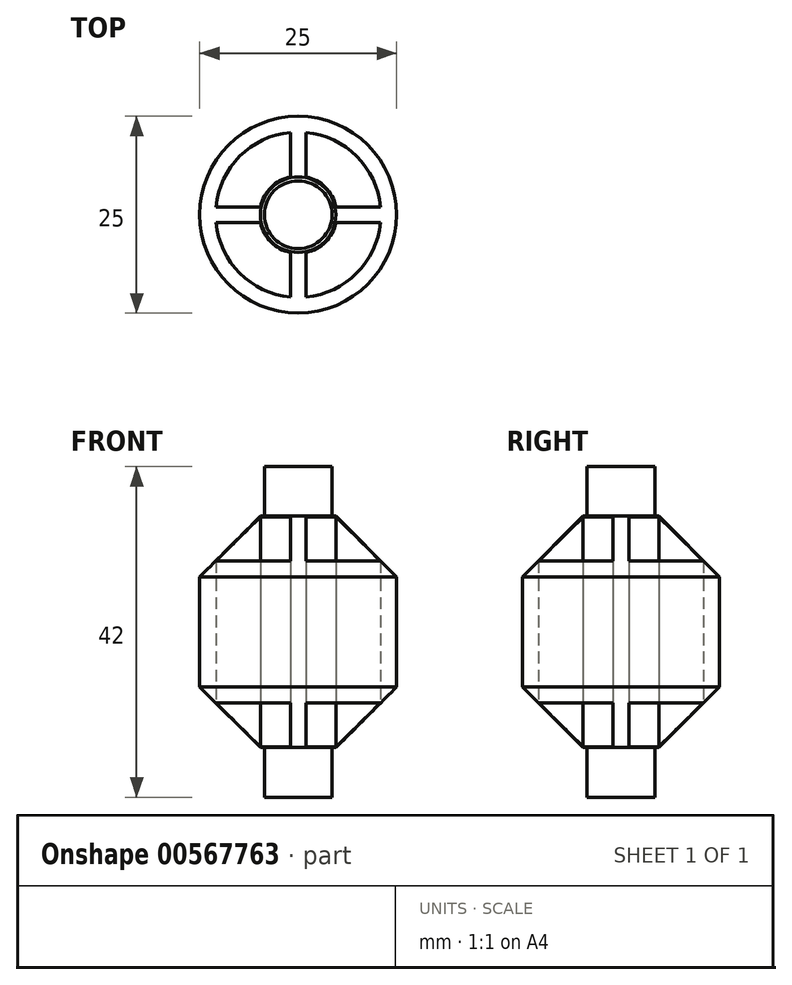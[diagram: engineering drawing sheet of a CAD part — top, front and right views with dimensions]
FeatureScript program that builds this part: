
annotation { "Feature Type Name" : "Feature", "Feature Type Description" : "" }
export const myFeature = defineFeature(function(context is Context, id is Id, definition is map)
    precondition{}
    {
        {
            var Q0;
            Q0=qCreatedBy(makeId("Top.planeOp"),FACE);
            var sketch = newSketch(context, id + "F0", { "sketchPlane" : qUnion([Q0])});
            skCircle(sketch, "E0", {"center": v(0, 0) * mm, "radius": 4.3 * mm});
            skCircle(sketch, "E1", {"center": v(0, 0) * mm, "radius": 2.3 * mm});
            skCircle(sketch, "E2", {"center": v(0, 0) * mm, "radius": 4.9 * mm});
            skCircle(sketch, "E3", {"center": v(0, 0) * mm, "radius": 12.5 * mm});
            skCircle(sketch, "E4", {"center": v(0, 0) * mm, "radius": 10.5 * mm});
            skLineSegment(sketch, "E5", {"start": v(-1, 4.8) * mm, "end": v(-1, 10.45) * mm});
            skLineSegment(sketch, "E6", {"start": v(1, 4.8) * mm, "end": v(1, 10.45) * mm});
            skLineSegment(sketch, "E7.1.0", {"start": v(-4.8, 1) * mm, "end": v(-10.45, 1) * mm});
            skLineSegment(sketch, "E7.1.1", {"start": v(-4.8, -1) * mm, "end": v(-10.45, -1) * mm});
            skLineSegment(sketch, "E7.2.0", {"start": v(-1, -4.8) * mm, "end": v(-1, -10.45) * mm});
            skLineSegment(sketch, "E7.2.1", {"start": v(1, -4.8) * mm, "end": v(1, -10.45) * mm});
            skLineSegment(sketch, "E7.3.0", {"start": v(4.8, -1) * mm, "end": v(10.45, -1) * mm});
            skLineSegment(sketch, "E7.3.1", {"start": v(4.8, 1) * mm, "end": v(10.45, 1) * mm});
            skSolve(sketch);
        }
        {
            var Q0;
            Q0=makeQuery(id+"F0.imprint","IMPRINT",FACE,{"disambiguationData":[TD([[makeQuery(id+"F0.imprint","IMPRINT",EDGE,{"derivedFrom":sQuery(id+"F0.wireOp",EDGE,"E0")}),1.0]])]});
            var Q1;
            Q1=makeQuery(id+"F0.imprint","IMPRINT",FACE,{"disambiguationData":[TD([[makeQuery(id+"F0.imprint","IMPRINT",EDGE,{"derivedFrom":sQuery(id+"F0.wireOp",EDGE,"E1")}),1.0]])]});
            extrude(context, id + "F1", {"entities" : qUnion([Q0, Q1]), "endBound" : BoundingType.SYMMETRIC, "depth" : 42 * mm, "offsetDistance" : 25 * mm});
        }
        {
            var Q0;
            Q0=makeQuery(id+"F0.imprint","IMPRINT",FACE,{"disambiguationData":[TD([[makeQuery(id+"F0.imprint","IMPRINT",EDGE,{"derivedFrom":sQuery(id+"F0.wireOp",EDGE,"E0")}),-1.0]])]});
            var Q1;
            {var subQ0=sQuery(id+"F0.wireOp",EDGE,"E7.1.0");Q1=makeQuery(id+"F0.imprint","IMPRINT",FACE,{"disambiguationData":[TD([[makeQuery(id+"F0.imprint","IMPRINT",EDGE,{"derivedFrom":subQ0}),1.0]])]});}
            var Q2;
            {var subQ0=sQuery(id+"F0.wireOp",EDGE,"E7.2.0");Q2=makeQuery(id+"F0.imprint","IMPRINT",FACE,{"disambiguationData":[TD([[makeQuery(id+"F0.imprint","IMPRINT",EDGE,{"derivedFrom":subQ0}),1.0]])]});}
            var Q3;
            {var subQ0=sQuery(id+"F0.wireOp",EDGE,"E7.3.0");Q3=makeQuery(id+"F0.imprint","IMPRINT",FACE,{"disambiguationData":[TD([[makeQuery(id+"F0.imprint","IMPRINT",EDGE,{"derivedFrom":subQ0}),1.0]])]});}
            var Q4;
            Q4=makeQuery(id+"F0.imprint","IMPRINT",FACE,{"disambiguationData":[TD([[makeQuery(id+"F0.imprint","IMPRINT",EDGE,{"derivedFrom":sQuery(id+"F0.wireOp",EDGE,"E3")}),1.0]])]});
            var Q5;
            {var subQ0=sQuery(id+"F0.wireOp",EDGE,"E5");Q5=makeQuery(id+"F0.imprint","IMPRINT",FACE,{"disambiguationData":[TD([[makeQuery(id+"F0.imprint","IMPRINT",EDGE,{"derivedFrom":subQ0}),-1.0]])]});}
            extrude(context, id + "F2", {"entities" : qUnion([Q0, Q1, Q2, Q3, Q4, Q5]), "operationType" : NewBodyOperationType.ADD, "endBound" : BoundingType.SYMMETRIC, "depth" : 29.4 * mm, "offsetDistance" : 25 * mm});
        }
        {
            var Q0;
            Q0=qCreatedBy(makeId("Front.planeOp"),FACE);
            var sketch = newSketch(context, id + "F3", { "sketchPlane" : qUnion([Q0])});
            skPoint(sketch, "E8.0", {"position": v(-4.8, 14.7) * mm});
            skPoint(sketch, "E8.1", {"position": v(-4.8, -14.7) * mm});
            skLineSegment(sketch, "E9", {"start": v(-4.8, -14.7) * mm, "end": v(-13.43, -6.07) * mm});
            skLineSegment(sketch, "E10", {"start": v(-13.43, -6.07) * mm, "end": v(-13.43, 6.07) * mm});
            skLineSegment(sketch, "E11", {"start": v(-13.43, 6.07) * mm, "end": v(-4.8, 14.7) * mm});
            skLineSegment(sketch, "E12", {"start": v(-4.8, -14.7) * mm, "end": v(-4.8, 14.7) * mm, "construction": true});
            skLineSegment(sketch, "E13", {"start": v(-13.43, -6.07) * mm, "end": v(-13.43, -14.7) * mm});
            skLineSegment(sketch, "E14", {"start": v(-13.43, -14.7) * mm, "end": v(-4.8, -14.7) * mm});
            skLineSegment(sketch, "E15", {"start": v(-13.43, 6.07) * mm, "end": v(-13.43, 14.7) * mm});
            skLineSegment(sketch, "E16", {"start": v(-13.43, 14.7) * mm, "end": v(-4.8, 14.7) * mm});
            skSolve(sketch);
        }
        {
            var Q0;
            Q0=makeQuery(id+"F3.imprint","IMPRINT",FACE,{"disambiguationData":[TD([[makeQuery(id+"F3.imprint","IMPRINT",EDGE,{"derivedFrom":sQuery(id+"F3.wireOp",EDGE,"E11")}),1.0]])]});
            var Q1;
            Q1=makeQuery(id+"F3.imprint","IMPRINT",FACE,{"disambiguationData":[TD([[makeQuery(id+"F3.imprint","IMPRINT",EDGE,{"derivedFrom":sQuery(id+"F3.wireOp",EDGE,"E9")}),1.0]])]});
            var Q2;
            Q2=makeQuery(id+"F2.opExtrude","CAP_EDGE",EDGE,{"disambiguationData":[OSD([sQuery(id+"F0.wireOp",EDGE,"E3")])],"isStart":true});
            revolve(context, id + "F4", {"operationType" : NewBodyOperationType.REMOVE, "entities" : qUnion([Q0, Q1]), "axis" : qUnion([Q2]), "revolveType" : RevolveType.FULL, "oppositeDirection" : true});
        }
    });
